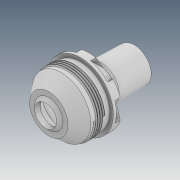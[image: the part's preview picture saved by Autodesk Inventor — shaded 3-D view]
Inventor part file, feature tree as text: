
AUTODESK INVENTOR PART (.ipt)
format: ipt  version: 2020 (Build 240168000, 168)  size: 499,712 bytes
history: native  units: mm
features: sketch x19, extrude x11, revolve x6, projected_geometry x6, chamfer x4, plane x4, helix x2, split x1, pattern_circular x1
ambient origin geometry x8: Origin, YZ Plane, XZ Plane, XY Plane, X Axis, Y Axis, Z Axis, Center Point
bodies: Solid1 (feature_tree)
feature tree (54):
  extrude  "Extrusion1"  Depth=2.0mm
  chamfer  "Chamfer1"  Distance=2.0mm
  revolve  "Revolution1"  [1 undecoded]
  extrude  "Extrusion2"  Depth=18.75mm
  sketch  "Sketch6"  dims[d17=1.6mm]
  helix  "Coil2"  [1 undecoded]
  chamfer  "Chamfer4"  Distance=10.0mm
  chamfer  "Chamfer5"  Distance=0.65mm Angle=45.0deg
  extrude  "Extrusion4"  Depth=42.0mm
  extrude  "Extrusion6"  Depth=3.3mm
  extrude  "Extrusion7"  Depth=1.2mm
  helix  "Coil3"  [1 undecoded]
  extrude  "Extrusion8"  Depth=3.0mm TaperAngle=0.0deg
  revolve  "Revolution2"  [1 undecoded]
  plane  "Work Plane2"
  split  "Split1"
  revolve  "Revolution3"  [1 undecoded]
  plane  "Work Plane3"
  plane  "Work Plane4"
  extrude  "Extrusion10"  Depth=11.335mm
  extrude  "Extrusion11"  Depth=11.335mm TaperAngle=0.0deg
  revolve  "Revolution4"  Angle=135.0deg
  extrude  "Extrusion12"  TaperAngle=90.0deg  [1 undecoded]
  revolve  "Revolution5"  [1 undecoded]
  plane  "Work Plane5"
  extrude  "Extrusion13"  Depth=11.335mm
  chamfer  "Chamfer7"  Distance=20.0mm
  pattern_circular  "Circular Pattern2"  [2 undecoded]
  extrude  "Extrusion14"  Depth=11.335mm
  revolve  "Revolution8"  Angle=90.0deg
  sketch  "Sketch1"  dims[d0=18.0mm d1=2.0mm d2=2.0mm d3=0.0mm]
  sketch  "Sketch4"  dims[d4=2.0mm d5=2.0mm d6=45.0deg d10=12.25mm]
  sketch  "Sketch5"  dims[d11=8.0mm d12=18.75mm d14=1.5mm]
  projected_geometry  "Projected Loop1"
  sketch  "Sketch8"  dims[d18=90.0deg d19=10.0mm d20=0.0mm]
  sketch  "Sketch9"  dims[d21=1.0mm]
  sketch  "Sketch10"  dims[d22=1.0mm]
  sketch  "Sketch11"  dims[d23=1.5mm]
  sketch  "Sketch12"  dims[d24=0.8mm]
  sketch  "Sketch13"  dims[d42=0.1mm]
  sketch  "Sketch14"  dims[d43=1.5mm]
  sketch  "Sketch16"  dims[d44=6.0mm d45=10.0mm d46=0.0mm d47=90.0deg d48=90.0deg d49=0.0mm d50=0.0mm d51=0.65mm d52=4.0mm d53=45.0deg]
  sketch  "Sketch17"  dims[d54=0.65mm d55=4.0mm d56=45.0deg d57=42.0mm]
  projected_geometry  "Projected Loop3"
  sketch  "Sketch18"  dims[d58=28.0mm d59=0.0mm d60=3.3mm]
  sketch  "Sketch19"  dims[d61=1.2mm d62=1.2mm d65=12.0mm d66=0.0mm]
  sketch  "Sketch20"  dims[d67=25.0mm d68=3.0mm d69=0.0mm]
  projected_geometry  "Projected Loop4"
  projected_geometry  "Projected Loop5"
  sketch  "Sketch21"  dims[d73=1.5mm d74=1.0mm]
  projected_geometry  "Projected Loop6"
  sketch  "Sketch22"  dims[d75=0.8mm d76=1.5mm]
  projected_geometry  "Projected Loop7"
  sketch  "Sketch23"  dims[d77=28.0mm d78=10.0mm d79=0.0mm d80=90.0deg d81=90.0deg d82=0.0mm d83=0.0mm d84=45.0mm d85=20.0mm d86=0.0mm d87=135.0deg d88=90.0deg d89=0.0mm d91=11.25mm d92=20.0mm d93=11.0mm d94=1.6mm d95=90.0deg d96=-20.0mm d108=-17.3mm d109=42.0mm d110=4.8mm d111=0.0mm d112=31.068147mm d113=21.0mm d115=2.8mm d116=0.0mm d117=0.473mm d118=90.0deg d119=2.8mm d120=0.0mm d121=135.0deg d122=90.0deg d123=-32.0mm d124=4.363323mm d125=10.0mm d126=0.0mm d127=6.5mm d128=9.75mm d129=45.0deg d130=60.0mm d131=360.0deg d133=22.5mm d134=20.0mm d135=0.0mm d137=15.0mm d138=10.81mm d139=11.185mm d140=21.0mm d141=11.335mm d142=1.2mm d143=360.0deg d144=90.0deg d147=90.0deg d148=90.0deg d70=0.5mm d71=0.872665mm d72=0.5mm d90=0.872665mm d136=0.872665mm]
note: 9 required parameter values undecoded (feature->parameter linkage not recoverable at this tier; creation-order binding heuristic only, values carry confidence <= 0.55)